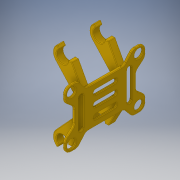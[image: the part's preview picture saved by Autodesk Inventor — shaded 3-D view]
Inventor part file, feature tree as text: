
AUTODESK INVENTOR PART (.ipt)
format: ipt  version: 2018 (Build 220112000, 112)  size: 815,616 bytes
history: native  units: in
note: dims shown in document units (in); Inventor stores cm internally (conversion verified against a paired STEP export)
features: fillet x11, extrude x4, sketch x4, projected_geometry x3, plane x1
ambient origin geometry x8: Origin, YZ Plane, XZ Plane, XY Plane, X Axis, Y Axis, Z Axis, Center Point
bodies: Solid1 (feature_tree)
feature tree (23):
  extrude  "Extrusion1"  Depth=0.0787in
  plane  "Work Plane1"
  extrude  "Extrusion2"  Depth=0.0197in
  extrude  "Extrusion3"  Depth=0.0197in
  extrude  "Extrusion4"  Depth=0.0197in
  fillet  "Fillet4"  Radius=0.2362in
  fillet  "Fillet5"  Radius=11.811in
  fillet  "Fillet6"  Radius=0.3543in
  fillet  "Fillet7"  Radius=0.3543in
  fillet  "Fillet8"  Radius=0.315in
  fillet  "Fillet9"  Radius=0.315in
  fillet  "Fillet10"  Radius=0.1575in
  fillet  "Fillet11"  Radius=0.1575in
  fillet  "Fillet12"  Radius=0.1575in
  fillet  "Fillet13"  Radius=3.937in
  fillet  "Fillet14"  Radius=0.0197in
  sketch  "Sketch1"  dims[d0=1.9291in d1=2.6772in d2=0.9646in d3=1.3386in d4=0.2953in d5=0.748in d6=1.122in d7=0.8933in d8=0.42in d9=0.1969in d10=0.315in d11=0.1575in d13=0.4606in d16=0.0787in d17=0.0in d21=0.6299in]
  sketch  "Sketch3"  dims[d22=0.6299in d23=0.0197in]
  projected_geometry  "Projected Loop1"
  sketch  "Sketch4"  dims[d24=0.0197in d25=1.2598in]
  projected_geometry  "Projected Loop2"
  sketch  "Sketch5"  dims[d26=0.1969in d27=0.0in d28=0.2362in d29=0.2362in d30=11.811in d31=0.0in d32=0.3543in d33=0.3543in d34=0.315in d35=0.315in d36=0.1575in d37=0.1575in d38=0.1575in d39=3.937in d40=0.0in d41=0.0197in d42=0.0197in d43=0.0197in d44=0.0197in d45=0.0197in d46=0.0197in d47=0.0197in d48=0.0197in d49=0.0197in d50=0.0197in d51=0.0197in]
  projected_geometry  "Projected Loop3"
